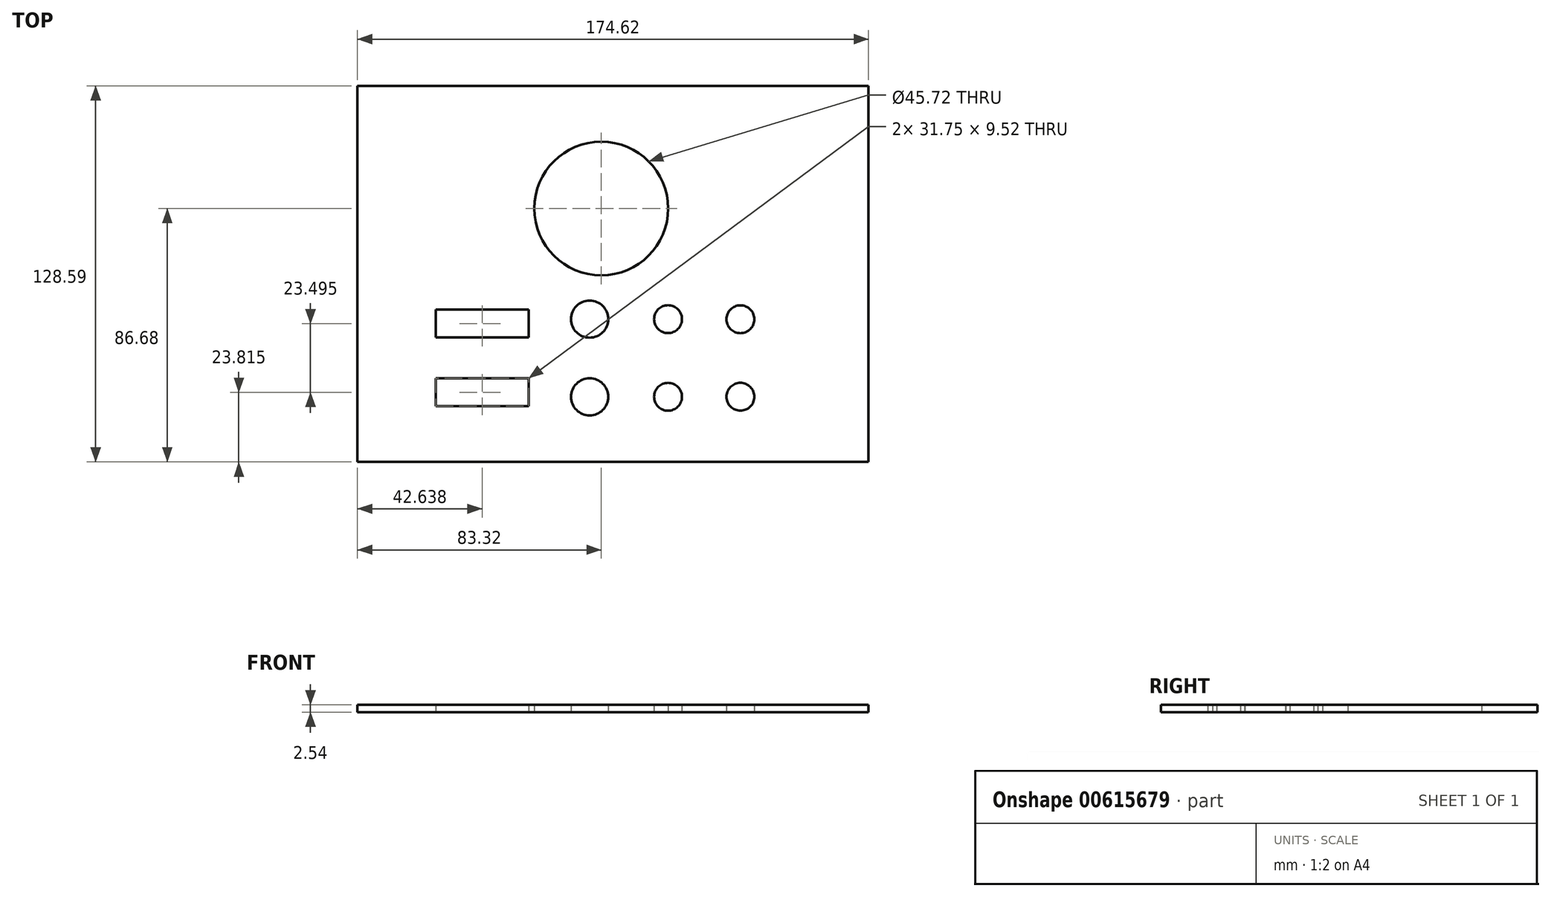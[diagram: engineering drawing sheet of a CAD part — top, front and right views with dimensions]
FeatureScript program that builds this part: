
annotation { "Feature Type Name" : "Feature", "Feature Type Description" : "" }
export const myFeature = defineFeature(function(context is Context, id is Id, definition is map)
    precondition{}
    {
        {
            var Q0;
            Q0=qCreatedBy(makeId("Top.planeOp"),FACE);
            var sketch = newSketch(context, id + "F0", { "sketchPlane" : qUnion([Q0])});
            skLineSegment(sketch, "E0.bottom", {"start": v(-83.32, 41.91) * mm, "end": v(91.3, 41.91) * mm});
            skLineSegment(sketch, "E0.top", {"start": v(-83.32, -86.68) * mm, "end": v(91.3, -86.68) * mm});
            skLineSegment(sketch, "E0.left", {"start": v(-83.32, 41.91) * mm, "end": v(-83.32, -86.68) * mm});
            skLineSegment(sketch, "E0.right", {"start": v(91.3, 41.91) * mm, "end": v(91.3, -86.68) * mm});
            skCircle(sketch, "E1", {"center": v(0, 0) * mm, "radius": 22.86 * mm});
            skLineSegment(sketch, "E2", {"start": v(0, 0) * mm, "end": v(-83.32, 0) * mm});
            skLineSegment(sketch, "E3", {"start": v(-83.32, 0) * mm, "end": v(91.3, 0) * mm});
            skLineSegment(sketch, "E4.bottom", {"start": v(-56.56, -58.1) * mm, "end": v(-24.8, -58.1) * mm});
            skLineSegment(sketch, "E4.top", {"start": v(-56.56, -67.63) * mm, "end": v(-24.8, -67.63) * mm});
            skLineSegment(sketch, "E4.left", {"start": v(-56.56, -58.1) * mm, "end": v(-56.56, -67.63) * mm});
            skLineSegment(sketch, "E4.right", {"start": v(-24.8, -58.1) * mm, "end": v(-24.8, -67.63) * mm});
            skCircle(sketch, "E5", {"center": v(22.82, -64.38) * mm, "radius": 4.76 * mm});
            skPoint(sketch, "E6.startSnap0", {"position": v(-56.56, -62.87) * mm});
            skCircle(sketch, "E7", {"center": v(47.54, -64.36) * mm, "radius": 4.76 * mm});
            skCircle(sketch, "E8", {"center": v(-3.97, -64.4) * mm, "radius": 6.35 * mm});
            skLineSegment(sketch, "E9", {"start": v(-83.32, -51.12) * mm, "end": v(91.3, -51.12) * mm});
            skCircle(sketch, "E10.MirrorC", {"center": v(-3.97, -37.83) * mm, "radius": 6.35 * mm});
            skCircle(sketch, "E11.MirrorC", {"center": v(22.82, -37.85) * mm, "radius": 4.76 * mm});
            skCircle(sketch, "E12.MirrorC", {"center": v(47.54, -37.87) * mm, "radius": 4.76 * mm});
            skLineSegment(sketch, "E13.MirrorCS", {"start": v(-56.56, -44.13) * mm, "end": v(-24.8, -44.13) * mm});
            skLineSegment(sketch, "E14.MirrorCS", {"start": v(-56.56, -34.6) * mm, "end": v(-24.8, -34.6) * mm});
            skLineSegment(sketch, "E15.MirrorCS", {"start": v(-24.8, -44.13) * mm, "end": v(-24.8, -34.6) * mm});
            skLineSegment(sketch, "E16.MirrorCS", {"start": v(-56.56, -44.13) * mm, "end": v(-56.56, -34.6) * mm});
            skSolve(sketch);
        }
        {
            var Q0;
            Q0 = qSketchRegion(id + "F0", true);
            extrude(context, id + "F1", {"entities" : qUnion([Q0]), "depth" : 2.54 * mm, "offsetDistance" : 25.4 * mm});
        }
    });
